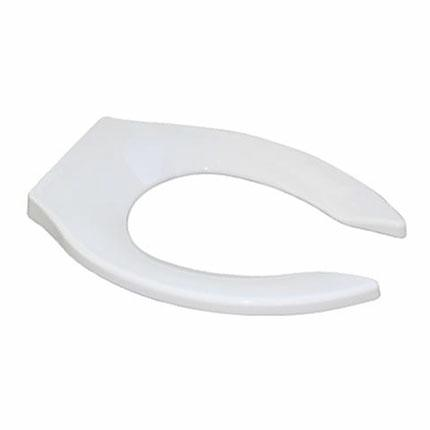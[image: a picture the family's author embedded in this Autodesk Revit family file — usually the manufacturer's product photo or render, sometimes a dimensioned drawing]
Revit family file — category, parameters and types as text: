
# Revit family: AF-2
name_source: partatom
category: Plumbing Fixtures
units: mm (PartAtom-declared; Revit-internal decimal feet)

## family parameters
Always vertical = Yes
Cut with Voids When Loaded = No
OmniClass Number = 23.45.00.00
OmniClass Title = Sanitary, Laundry, and Cleaning Equipment
Part Type = Normal
Room Calculation Point = No
Round Connector Dimension = Use Diameter
Shared = Yes
Work Plane-Based = No

## types (1)
- AF-2
    Data Sheet = https://www.helvex.com.mx
    Default Elevation = 0"
    Description = Asiento Elongado Frente Abierto para Taza Fluxómetro
    Instructive = https://www.helvex.com.mx
    Manufacturer = HELVEX
    Model = AF-2
    Placement Height = 14.5"
    Polypropylene = Polypropylene
    Total Height = 2"
    Total Length = 19"
    Total Width = 14"
    Type Comments = SANIVEX
    Type Image = AF-2.jpg
    URL = https://www.helvex.com.mx

## geometry (parser evidence)
native form markers: Sweep x3
no freeform markers — native parametric forms only
